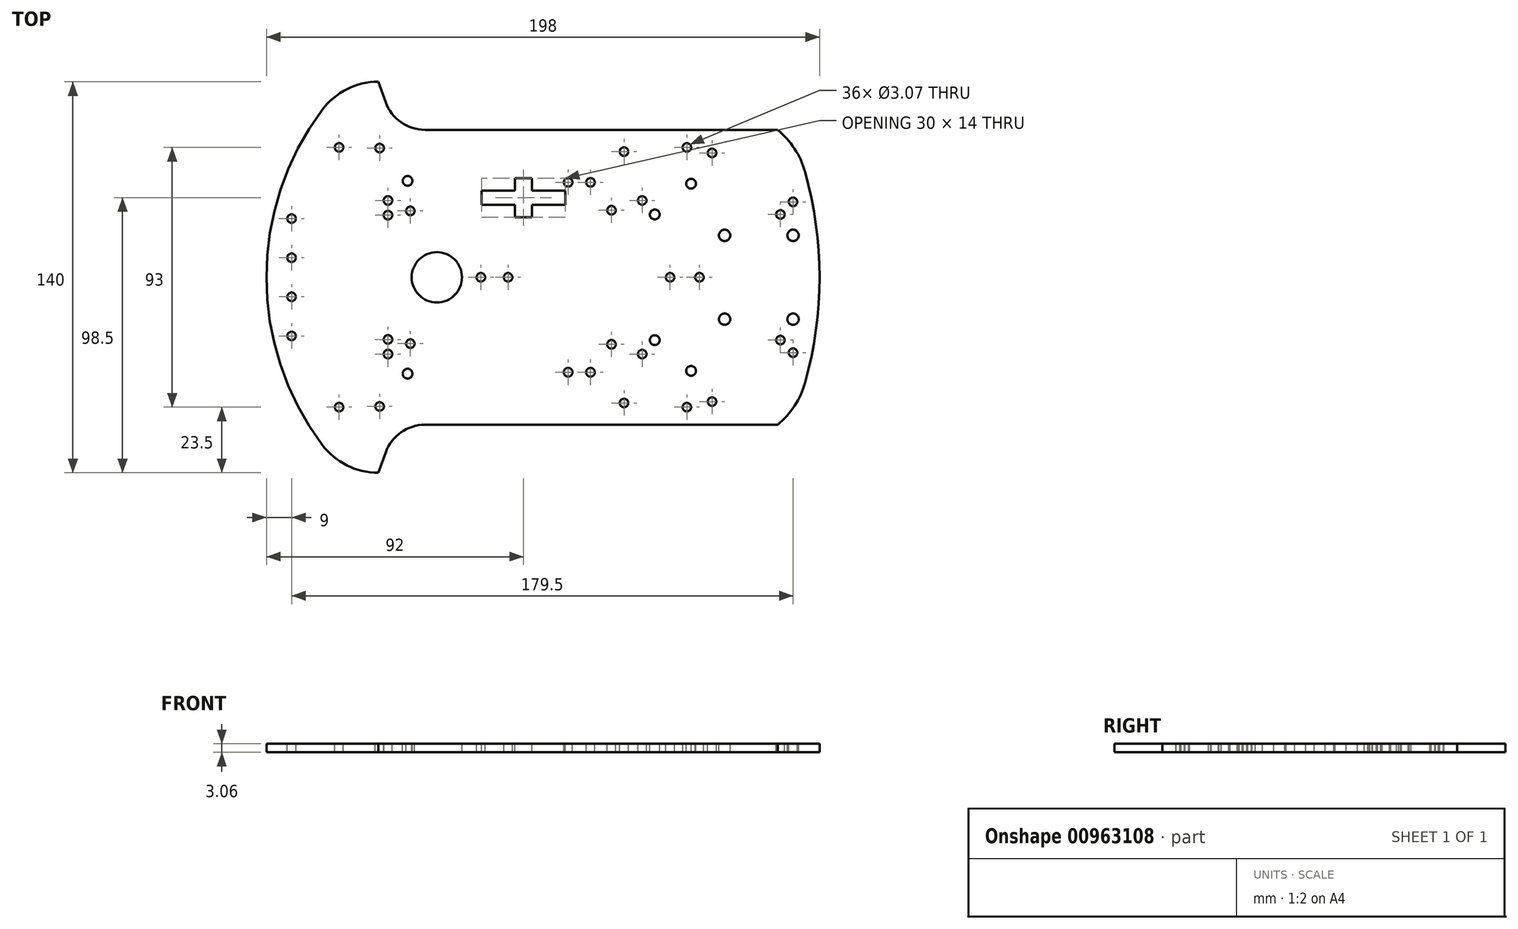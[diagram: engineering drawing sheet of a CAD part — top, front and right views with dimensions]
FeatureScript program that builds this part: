
annotation { "Feature Type Name" : "Feature", "Feature Type Description" : "" }
export const myFeature = defineFeature(function(context is Context, id is Id, definition is map)
    precondition{}
    {
        {
            var Q0;
            Q0=qCreatedBy(makeId("Top.planeOp"),FACE);
            var sketch = newSketch(context, id + "F0", { "sketchPlane" : qUnion([Q0])});
            skLineSegment(sketch, "E0", {"start": v(-4.24, 52.8) * mm, "end": v(122, 52.8) * mm});
            skLineSegment(sketch, "E1", {"start": v(-61, 0) * mm, "end": v(137, 0) * mm});
            skLineSegment(sketch, "E2", {"start": v(137, 0) * mm, "end": v(137, 80.6) * mm, "construction": true});
            skArc(sketch, "E3", {"start": v(-41, 60) * mm, "mid": v(-55.87, 31.62) * mm, "end": v(-61, 0) * mm});
            skArc(sketch, "E4", {"start": v(-21, 70) * mm, "mid": v(-32.18, 67.36) * mm, "end": v(-41, 60) * mm});
            skArc(sketch, "E5", {"start": v(-18.33, 62.67) * mm, "mid": v(-12.84, 55.51) * mm, "end": v(-4.24, 52.8) * mm});
            skLineSegment(sketch, "E6", {"start": v(-18.33, 62.67) * mm, "end": v(-21, 70) * mm});
            skArc(sketch, "E7", {"start": v(137, 0) * mm, "mid": v(135.7, 19.04) * mm, "end": v(131.82, 37.72) * mm});
            skArc(sketch, "E8", {"start": v(131.82, 37.72) * mm, "mid": v(128.07, 46.02) * mm, "end": v(122, 52.8) * mm});
            skLineSegment(sketch, "E9", {"start": v(-21, 70) * mm, "end": v(66.23, 70) * mm, "construction": true});
            skSolve(sketch);
        }
        {
            var Q0;
            Q0 = qSketchRegion(id + "F0", true);
            extrude(context, id + "F1", {"entities" : qUnion([Q0]), "depth" : 3.05 * mm, "offsetDistance" : 25 * mm, "symmetric" : true});
        }
        {
            var Q0;
            {var subQ0=makeQuery(id+"F1.opExtrude","CAP_FACE",FACE,{"disambiguationData":[OSD([sQuery(id+"F0.wireOp",EDGE,"E0"),sQuery(id+"F0.wireOp",EDGE,"E1"),sQuery(id+"F0.wireOp",EDGE,"E3"),sQuery(id+"F0.wireOp",EDGE,"E4"),sQuery(id+"F0.wireOp",EDGE,"E5"),sQuery(id+"F0.wireOp",EDGE,"E6"),sQuery(id+"F0.wireOp",EDGE,"E7"),sQuery(id+"F0.wireOp",EDGE,"E8")])],"isStart":false});Q0=makeQuery(id+"F4.boolean.opBoolean","MERGE",FACE,{"derivedFrom":[subQ0,makeQuery(id+"F4.opPattern","COPY",FACE,{"derivedFrom":subQ0,"instanceName":"1"})]});}
            var sketch = newSketch(context, id + "F2", { "sketchPlane" : qUnion([Q0])});
            skCircle(sketch, "E10", {"center": v(0, 0) * mm, "radius": 9 * mm});
            skCircle(sketch, "E11", {"center": v(-52, 21) * mm, "radius": 1.53 * mm});
            skCircle(sketch, "E12", {"center": v(-52, 7) * mm, "radius": 1.53 * mm});
            skLineSegment(sketch, "E13", {"start": v(0, 0) * mm, "end": v(-70.4, 0) * mm, "construction": true});
            skCircle(sketch, "E14", {"center": v(-35, 46.5) * mm, "radius": 1.53 * mm});
            skCircle(sketch, "E15", {"center": v(-20.5, 46.25) * mm, "radius": 1.53 * mm});
            skCircle(sketch, "E16", {"center": v(-17.5, 27.5) * mm, "radius": 1.53 * mm});
            skCircle(sketch, "E17", {"center": v(-17.5, 22.25) * mm, "radius": 1.53 * mm});
            skCircle(sketch, "E18", {"center": v(-10.5, 34.5) * mm, "radius": 1.75 * mm});
            skCircle(sketch, "E19", {"center": v(-9.5, 23.75) * mm, "radius": 1.53 * mm});
            skCircle(sketch, "E20", {"center": v(15.75, 0) * mm, "radius": 1.53 * mm});
            skCircle(sketch, "E21", {"center": v(25.5, 0) * mm, "radius": 1.53 * mm});
            skCircle(sketch, "E22", {"center": v(47, 34) * mm, "radius": 1.53 * mm});
            skCircle(sketch, "E23", {"center": v(55, 34) * mm, "radius": 1.53 * mm});
            skCircle(sketch, "E24", {"center": v(62.5, 24) * mm, "radius": 1.53 * mm});
            skCircle(sketch, "E25", {"center": v(67, 45) * mm, "radius": 1.53 * mm});
            skCircle(sketch, "E26", {"center": v(73.5, 27.5) * mm, "radius": 1.53 * mm});
            skCircle(sketch, "E27", {"center": v(78, 22.5) * mm, "radius": 1.75 * mm});
            skCircle(sketch, "E28", {"center": v(83.5, 0) * mm, "radius": 1.53 * mm});
            skCircle(sketch, "E29", {"center": v(94, 0) * mm, "radius": 1.53 * mm});
            skCircle(sketch, "E30", {"center": v(91, 33.5) * mm, "radius": 1.75 * mm});
            skCircle(sketch, "E31", {"center": v(89.5, 46.5) * mm, "radius": 1.53 * mm});
            skCircle(sketch, "E32", {"center": v(98.5, 44.5) * mm, "radius": 1.53 * mm});
            skCircle(sketch, "E33", {"center": v(103, 15) * mm, "radius": 2.04 * mm});
            skCircle(sketch, "E34", {"center": v(123, 22.5) * mm, "radius": 1.53 * mm});
            skCircle(sketch, "E35", {"center": v(127.5, 27) * mm, "radius": 1.53 * mm});
            skCircle(sketch, "E36", {"center": v(127.5, 15) * mm, "radius": 2.04 * mm});
            skSolve(sketch);
        }
        {
            var Q0;
            Q0 = qSketchRegion(id + "F2", true);
            extrude(context, id + "F3", {"entities" : qUnion([Q0]), "operationType" : NewBodyOperationType.REMOVE, "endBound" : BoundingType.THROUGH_ALL, "oppositeDirection" : true, "depth" : 25 * mm, "offsetDistance" : 25 * mm});
        }
        {
            var Q0;
            Q0=makeQuery(id+"F1.opExtrude","SWEPT_BODY",BODY,{"disambiguationData":[OSD([sQuery(id+"F0.wireOp",EDGE,"E0"),sQuery(id+"F0.wireOp",EDGE,"E1"),sQuery(id+"F0.wireOp",EDGE,"E3"),sQuery(id+"F0.wireOp",EDGE,"E4"),sQuery(id+"F0.wireOp",EDGE,"E5"),sQuery(id+"F0.wireOp",EDGE,"E6"),sQuery(id+"F0.wireOp",EDGE,"E7"),sQuery(id+"F0.wireOp",EDGE,"E8")])]});
            var Q1;
            Q1=makeQuery(id+"F1.opExtrude","SWEPT_FACE",FACE,{"disambiguationData":[OSD([sQuery(id+"F0.wireOp",EDGE,"E1")])]});
            mirror(context, id + "F4", {"operationType" : NewBodyOperationType.ADD, "entities" : qUnion([Q0]), "mirrorPlane" : qUnion([Q1])});
        }
        {
            var Q0;
            {var subQ0=makeQuery(id+"F1.opExtrude","CAP_FACE",FACE,{"disambiguationData":[OSD([sQuery(id+"F0.wireOp",EDGE,"E0"),sQuery(id+"F0.wireOp",EDGE,"E1"),sQuery(id+"F0.wireOp",EDGE,"E3"),sQuery(id+"F0.wireOp",EDGE,"E4"),sQuery(id+"F0.wireOp",EDGE,"E5"),sQuery(id+"F0.wireOp",EDGE,"E6"),sQuery(id+"F0.wireOp",EDGE,"E7"),sQuery(id+"F0.wireOp",EDGE,"E8")])],"isStart":false});Q0=makeQuery(id+"F4.boolean.opBoolean","MERGE",FACE,{"derivedFrom":[subQ0,makeQuery(id+"F4.opPattern","COPY",FACE,{"derivedFrom":subQ0,"instanceName":"1"})]});}
            var sketch = newSketch(context, id + "F5", { "sketchPlane" : qUnion([Q0])});
            skLineSegment(sketch, "E37", {"start": v(34, 31) * mm, "end": v(46, 31) * mm});
            skLineSegment(sketch, "E38", {"start": v(46, 31) * mm, "end": v(46, 26) * mm});
            skLineSegment(sketch, "E39", {"start": v(46, 26) * mm, "end": v(34, 26) * mm});
            skLineSegment(sketch, "E40", {"start": v(34, 26) * mm, "end": v(34, 21.5) * mm});
            skLineSegment(sketch, "E41", {"start": v(34, 21.5) * mm, "end": v(28, 21.5) * mm});
            skLineSegment(sketch, "E42", {"start": v(28, 21.5) * mm, "end": v(28, 26) * mm});
            skLineSegment(sketch, "E43", {"start": v(28, 26) * mm, "end": v(16, 26) * mm});
            skLineSegment(sketch, "E44", {"start": v(16, 26) * mm, "end": v(16, 31) * mm});
            skLineSegment(sketch, "E45", {"start": v(16, 31) * mm, "end": v(28, 31) * mm});
            skLineSegment(sketch, "E46", {"start": v(28, 31) * mm, "end": v(28, 35.5) * mm});
            skLineSegment(sketch, "E47", {"start": v(28, 35.5) * mm, "end": v(34, 35.5) * mm});
            skLineSegment(sketch, "E48", {"start": v(34, 35.5) * mm, "end": v(34, 31) * mm});
            skSolve(sketch);
        }
        {
            var Q0;
            Q0 = qSketchRegion(id + "F5", true);
            extrude(context, id + "F6", {"entities" : qUnion([Q0]), "operationType" : NewBodyOperationType.REMOVE, "endBound" : BoundingType.UP_TO_NEXT, "oppositeDirection" : true, "depth" : 25 * mm, "offsetDistance" : 25 * mm});
        }
    });
